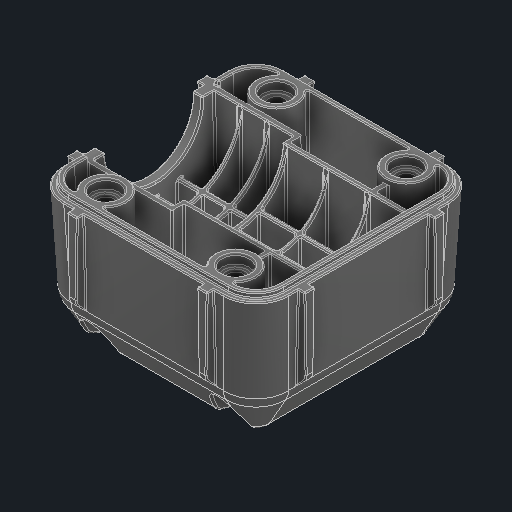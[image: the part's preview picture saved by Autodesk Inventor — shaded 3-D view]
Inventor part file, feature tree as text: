
AUTODESK INVENTOR PART (.ipt)
format: ipt  version: 2024.2 (Build 282272000, 272)  size: 2,868,736 bytes
history: native  units: in
note: dims shown in document units (in); Inventor stores cm internally (conversion verified against a paired STEP export)
features: fillet x1
ambient origin geometry x8: Origin, YZ Plane, XZ Plane, XY Plane, X Axis, Y Axis, Z Axis, Center Point
bodies: Solid1 (feature_tree)
feature tree (1):
  fillet  "Fillet32"  [1 undecoded]
note: 1 required parameter value undecoded (feature->parameter linkage not recoverable at this tier; creation-order binding heuristic only, values carry confidence <= 0.55)
